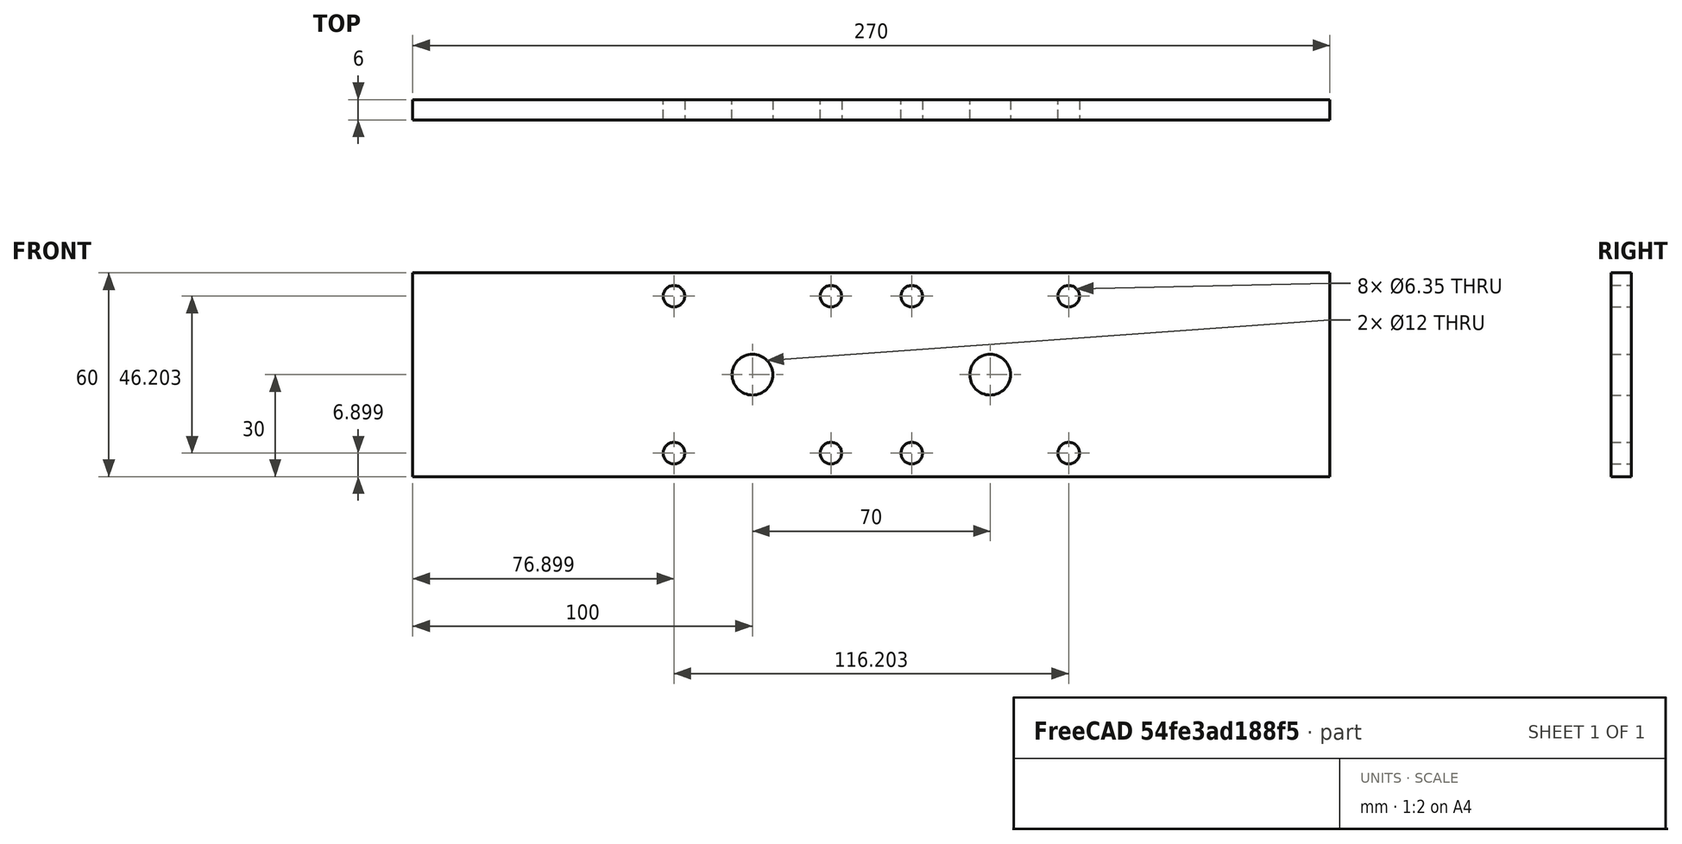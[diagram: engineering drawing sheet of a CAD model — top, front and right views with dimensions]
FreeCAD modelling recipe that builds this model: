
FCSTD DOCUMENT  (FreeCAD 0.18R4 (GitTag))
Label: soporte_motor
License: All rights reserved
LicenseURL: http://en.wikipedia.org/wiki/All_rights_reserved
objects: Sketcher::SketchObject×1, PartDesign::Pad×1, PartDesign::Body×1
note: 4 computed .brp shape members not serialized (recipe doc carries the construction recipe); baked Part::Feature solids carry a one-line shape summary decoded from their .brp

FEATURE [Sketcher::SketchObject] Sketch
  MapMode = 5
  Placement = pos=(0,0,0) rot=(1,0,0;1.5708rad)
  Support = -> [XZ_Plane]
  sketch-geometry (14):
    g0: LineSegment StartX=0 StartY=0 StartZ=0 EndX=270 EndY=0 EndZ=0
    g1: LineSegment StartX=270 StartY=0 StartZ=0 EndX=270 EndY=60 EndZ=0
    g2: LineSegment StartX=270 StartY=60 StartZ=0 EndX=0 EndY=60 EndZ=0
    g3: LineSegment StartX=0 StartY=60 StartZ=0 EndX=0 EndY=0 EndZ=0
    g4: Circle CenterX=100 CenterY=30 CenterZ=0 NormalX=0 NormalY=0 NormalZ=1 AngleXU=0 Radius=6
    g5: Circle CenterX=123.101 CenterY=53.1013 CenterZ=0 NormalX=0 NormalY=0 NormalZ=1 AngleXU=0 Radius=3.175
    g6: Circle CenterX=76.8987 CenterY=53.1013 CenterZ=0 NormalX=0 NormalY=0 NormalZ=1 AngleXU=0 Radius=3.175
    g7: Circle CenterX=76.8987 CenterY=6.8987 CenterZ=0 NormalX=0 NormalY=0 NormalZ=1 AngleXU=0 Radius=3.175
    g8: Circle CenterX=123.101 CenterY=6.8987 CenterZ=0 NormalX=0 NormalY=0 NormalZ=1 AngleXU=0 Radius=3.175
    g9: Circle CenterX=170 CenterY=30 CenterZ=0 NormalX=0 NormalY=0 NormalZ=1 AngleXU=0 Radius=6
    g10: Circle CenterX=193.101 CenterY=53.1013 CenterZ=0 NormalX=0 NormalY=0 NormalZ=1 AngleXU=0 Radius=3.175
    g11: Circle CenterX=146.899 CenterY=53.1013 CenterZ=0 NormalX=0 NormalY=0 NormalZ=1 AngleXU=0 Radius=3.175
    g12: Circle CenterX=146.899 CenterY=6.8987 CenterZ=0 NormalX=0 NormalY=0 NormalZ=1 AngleXU=0 Radius=3.175
    g13: Circle CenterX=193.101 CenterY=6.8987 CenterZ=0 NormalX=0 NormalY=0 NormalZ=1 AngleXU=0 Radius=3.175
  constraints (41):
    c: Coincident(g0,g1)
    c: Coincident(g1,g2)
    c: Coincident(g2,g3)
    c: Coincident(g3,g0)
    c: Horizontal(g0)
    c: Horizontal(g2)
    c: Vertical(g1)
    c: Vertical(g3)
    c: Coincident(g0,g-1)
    c: DistanceX(g0,g0) = 270
    c: DistanceY(g3,g3) = 60
    c: Distance(g4,g2) = 30
    c: Distance(g4,g3) = 100
    c: Radius(g4) = 6
    c: Radius(g5) = 3.175
    c: Radius(g6) = 3.175
    c: Radius(g8) = 3.175
    c: Radius(g7) = 3.175
    c: DistanceX(g7,g8) = 46.2026
    c: DistanceX(g6,g5) = 46.2026
    c: DistanceX(g6,g4) = 23.1013
    c: DistanceX(g7,g4) = 23.1013
    c: DistanceY(g8,g5) = 46.2026
    c: DistanceY(g8,g4) = 23.1013
    c: DistanceY(g7,g6) = 46.2026
    c: DistanceY(g4,g6) = 23.1013
    c: Equal(g4,g9) = 6
    c: Equal(g5,g10) = 3.175
    c: Equal(g6,g11) = 3.175
    c: Equal(g8,g13) = 3.175
    c: Equal(g7,g12) = 3.175
    c: DistanceX(g12,g13) = 46.2026
    c: DistanceX(g11,g10) = 46.2026
    c: DistanceX(g11,g9) = 23.1013
    c: DistanceX(g12,g9) = 23.1013
    c: DistanceY(g13,g10) = 46.2026
    c: DistanceY(g13,g9) = 23.1013
    c: DistanceY(g12,g11) = 46.2026
    c: DistanceY(g9,g11) = 23.1013
    c: Distance(g9,g3) = 170
    c: Distance(g9,g2) = 30
FEATURE [PartDesign::Pad] Pad
  Length = 6
  Length2 = 100
  Placement = pos=(0,0,0) rot=(1,0,0;1.5708rad)
  Profile = -> Sketch
  Type = 0
FEATURE [PartDesign::Body] Body
  Group = -> [Sketch,Pad]
  Origin = -> Origin
  Tip = -> Pad
